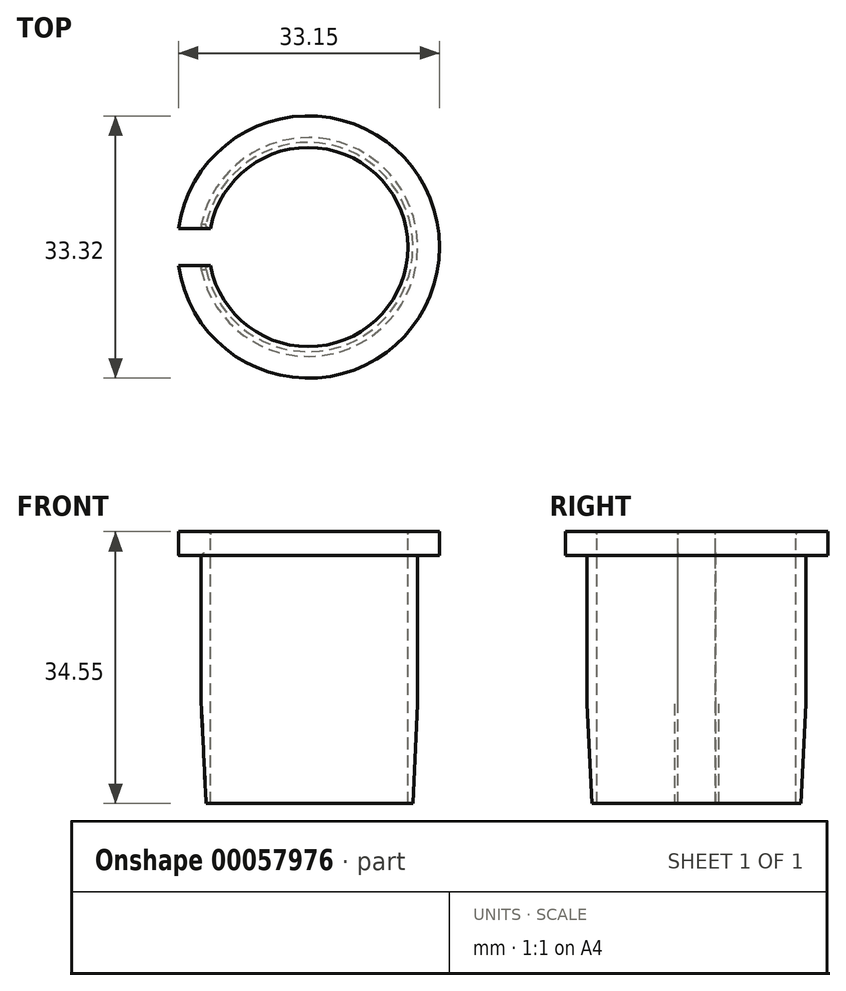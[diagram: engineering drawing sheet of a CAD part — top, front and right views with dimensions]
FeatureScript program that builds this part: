
annotation { "Feature Type Name" : "Feature", "Feature Type Description" : "" }
export const myFeature = defineFeature(function(context is Context, id is Id, definition is map)
    precondition{}
    {
        {
            var Q0;
            Q0=qCreatedBy(makeId("Right.planeOp"),FACE);
            var sketch = newSketch(context, id + "F0", { "sketchPlane" : qUnion([Q0])});
            skLineSegment(sketch, "E0", {"start": v(0, 34.7) * mm, "end": v(0, -25.4) * mm, "construction": true});
            skLineSegment(sketch, "E1", {"start": v(-12.65, 34.7) * mm, "end": v(-16.66, 34.7) * mm});
            skLineSegment(sketch, "E2", {"start": v(-16.66, 34.7) * mm, "end": v(-16.66, 31.65) * mm});
            skLineSegment(sketch, "E3", {"start": v(-16.66, 31.65) * mm, "end": v(-13.9, 31.65) * mm});
            skLineSegment(sketch, "E4", {"start": v(-13.9, 31.65) * mm, "end": v(-13.9, 12.85) * mm});
            skLineSegment(sketch, "E5", {"start": v(-16.66, -24.6) * mm, "end": v(-16.66, -24.61) * mm});
            skLineSegment(sketch, "E6", {"start": v(-12.65, 34.7) * mm, "end": v(-12.65, 0.15) * mm});
            skPoint(sketch, "E7.visualSharp", {"position": v(-12.65, 34.7) * mm});
            skPoint(sketch, "E8.visualSharp", {"position": v(-16.66, 34.7) * mm});
            skPoint(sketch, "E9.visualSharp", {"position": v(-16.66, 31.65) * mm});
            skLineSegment(sketch, "E10", {"start": v(-12.65, 0.15) * mm, "end": v(-13.28, 0.15) * mm});
            skLineSegment(sketch, "E11", {"start": v(-13.9, 12.85) * mm, "end": v(-13.28, 0.15) * mm});
            skSolve(sketch);
        }
        {
            var Q0;
            Q0=qSketchRegion(id+"F0",true);
            var Q1;
            Q1=sQuery(id+"F0.wireOp",EDGE,"E0");
            revolve(context, id + "F1", {"entities" : qUnion([Q0]), "axis" : qUnion([Q1]), "revolveType" : RevolveType.FULL});
        }
        {
            var Q0;
            Q0=qCreatedBy(makeId("Top.planeOp"),FACE);
            var sketch = newSketch(context, id + "F2", { "sketchPlane" : qUnion([Q0])});
            skLineSegment(sketch, "E12.rect.bottom", {"start": v(-25.4, 2.37) * mm, "end": v(-0.25, 2.37) * mm});
            skLineSegment(sketch, "E12.rect.top", {"start": v(-25.4, -2.37) * mm, "end": v(-0.25, -2.37) * mm});
            skLineSegment(sketch, "E12.rect.left", {"start": v(-25.4, 2.37) * mm, "end": v(-25.4, -2.37) * mm});
            skPoint(sketch, "E12.rect.middle", {"position": v(0, 0) * mm});
            skLineSegment(sketch, "E13", {"start": v(-0.25, -2.37) * mm, "end": v(-0.25, 2.37) * mm});
            skSolve(sketch);
        }
        {
            var Q0;
            Q0=qSketchRegion(id+"F2",true);
            extrude(context, id + "F3", {"entities" : qUnion([Q0]), "operationType" : NewBodyOperationType.REMOVE, "endBound" : BoundingType.THROUGH_ALL, "depth" : 50.8 * mm});
        }
        {
            var Q0;
            Q0=makeQuery(id+"F3.boolean.opBoolean","INTERSECT",EDGE,{"derivedFrom":[makeQuery(id+"F1.opRevolve","SWEPT_FACE",FACE,{"disambiguationData":[OSD([sQuery(id+"F0.wireOp",EDGE,"E11")])]}),makeQuery(id+"F3.opExtrude","SWEPT_FACE",FACE,{"disambiguationData":[OSD([sQuery(id+"F2.wireOp",EDGE,"E12.rect.top")])]})]});
            var Q1;
            Q1=makeQuery(id+"F3.boolean.opBoolean","INTERSECT",EDGE,{"derivedFrom":[makeQuery(id+"F1.opRevolve","SWEPT_FACE",FACE,{"disambiguationData":[OSD([sQuery(id+"F0.wireOp",EDGE,"E4")])]}),makeQuery(id+"F3.opExtrude","SWEPT_FACE",FACE,{"disambiguationData":[OSD([sQuery(id+"F2.wireOp",EDGE,"E12.rect.top")])]})]});
            var Q2;
            Q2=makeQuery(id+"F3.boolean.opBoolean","INTERSECT",EDGE,{"derivedFrom":[makeQuery(id+"F1.opRevolve","SWEPT_FACE",FACE,{"disambiguationData":[OSD([sQuery(id+"F0.wireOp",EDGE,"E11")])]}),makeQuery(id+"F3.opExtrude","SWEPT_FACE",FACE,{"disambiguationData":[OSD([sQuery(id+"F2.wireOp",EDGE,"E12.rect.bottom")])]})]});
            var Q3;
            Q3=makeQuery(id+"F3.boolean.opBoolean","INTERSECT",EDGE,{"derivedFrom":[makeQuery(id+"F1.opRevolve","SWEPT_FACE",FACE,{"disambiguationData":[OSD([sQuery(id+"F0.wireOp",EDGE,"E4")])]}),makeQuery(id+"F3.opExtrude","SWEPT_FACE",FACE,{"disambiguationData":[OSD([sQuery(id+"F2.wireOp",EDGE,"E12.rect.bottom")])]})]});
            var Q4;
            Q4=makeQuery(id+"F3.boolean.opBoolean","INTERSECT",EDGE,{"derivedFrom":[makeQuery(id+"F1.opRevolve","SWEPT_FACE",FACE,{"disambiguationData":[OSD([sQuery(id+"F0.wireOp",EDGE,"E3")])]}),makeQuery(id+"F3.opExtrude","SWEPT_FACE",FACE,{"disambiguationData":[OSD([sQuery(id+"F2.wireOp",EDGE,"E12.rect.top")])]})]});
            var Q5;
            Q5=makeQuery(id+"F3.boolean.opBoolean","INTERSECT",EDGE,{"derivedFrom":[makeQuery(id+"F1.opRevolve","SWEPT_FACE",FACE,{"disambiguationData":[OSD([sQuery(id+"F0.wireOp",EDGE,"E3")])]}),makeQuery(id+"F3.opExtrude","SWEPT_FACE",FACE,{"disambiguationData":[OSD([sQuery(id+"F2.wireOp",EDGE,"E12.rect.bottom")])]})]});
            var Q6;
            Q6=makeQuery(id+"F1.opRevolve","SWEPT_EDGE",EDGE,{"disambiguationData":[OSD([sQuery(id+"F0.wireOp",EDGE,"E1"),sQuery(id+"F0.wireOp",EDGE,"E6")])]});
            var Q7;
            Q7=makeQuery(id+"F1.opRevolve","SWEPT_EDGE",EDGE,{"disambiguationData":[OSD([sQuery(id+"F0.wireOp",EDGE,"E4"),sQuery(id+"F0.wireOp",EDGE,"E11")])]});
            fillet(context, id + "F4", {"entities" : qUnion([Q0, Q1, Q2, Q3, Q4, Q5, Q6, Q7]), "radius" : 0.38 * mm, "tangentPropagation" : true, "allowEdgeOverflow" : false});
        }
    });
